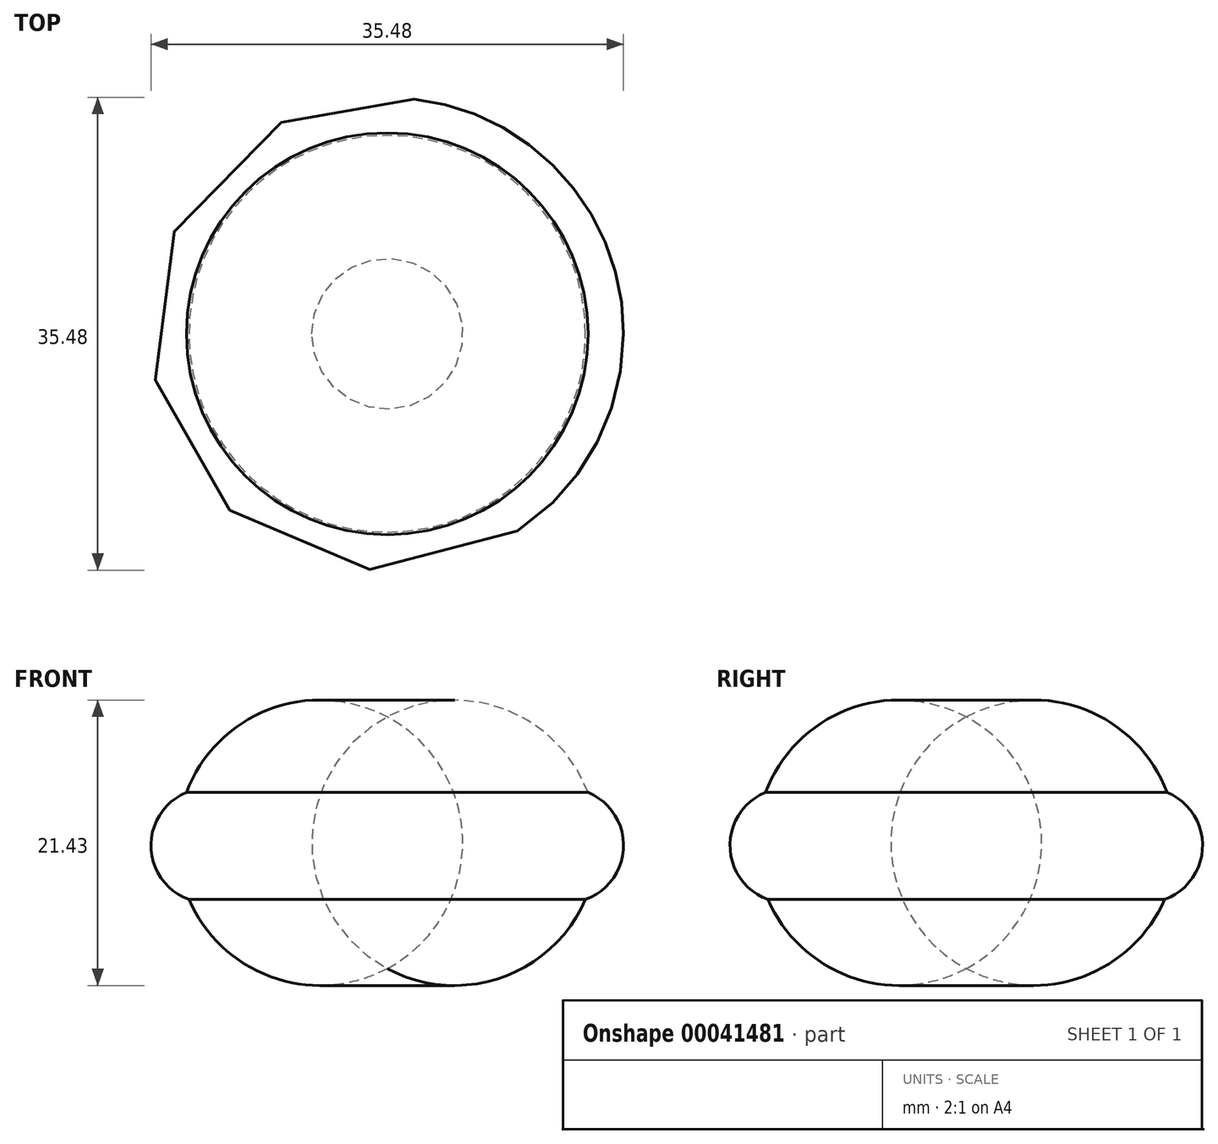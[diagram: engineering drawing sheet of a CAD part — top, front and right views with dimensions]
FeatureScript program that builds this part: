
annotation { "Feature Type Name" : "Feature", "Feature Type Description" : "" }
export const myFeature = defineFeature(function(context is Context, id is Id, definition is map)
    precondition{}
    {
        {
            var Q0;
            Q0=qCreatedBy(makeId("Front.planeOp"),FACE);
            var sketch = newSketch(context, id + "F0", { "sketchPlane" : qUnion([Q0])});
            skArc(sketch, "E0", {"start": v(14.89, -5.58) * mm, "mid": v(17.74, -1.63) * mm, "end": v(15.08, 2.45) * mm});
            skArc(sketch, "E1", {"start": v(14.89, -5.58) * mm, "mid": v(15.76, -1.59) * mm, "end": v(15.08, 2.45) * mm});
            skLineSegment(sketch, "E2", {"start": v(0, 18.31) * mm, "end": v(0, -19.1) * mm});
            skSolve(sketch);
        }
        {
            var Q0;
            Q0=makeQuery(id+"F0.imprint","IMPRINT",FACE,{"disambiguationData":[TD([[makeQuery(id+"F0.imprint","IMPRINT",EDGE,{"derivedFrom":sQuery(id+"F0.wireOp",EDGE,"E0")}),1.0]])]});
            var Q1;
            Q1=sQuery(id+"F0.wireOp",EDGE,"E2");
            revolve(context, id + "F1", {"entities" : qUnion([Q0]), "axis" : qUnion([Q1]), "revolveType" : RevolveType.FULL});
        }
    });
